# Revit family: Садово-парковая скамейка «Мой Парк NOVA»
name_source: partatom
category: Мебель
revit_build: Autodesk Revit 2017 (Build: 20160225_1515(x64)
units: mm (PartAtom-declared; Revit-internal decimal feet)

## family parameters
Всегда вертикально = Да
Заголовок OmniClass = General Furniture and Specialties
На основе рабочей плоскости = Нет
Номер OmniClass = 23.40.20.00
Общий = Нет
При загрузке вырезать с полостями = Нет
Точка расчета площади = Нет

## types (6) — shared parameters
ADSK_Код изделия = 8464
ADSK_Материал доски = <По категории>
ADSK_Материал опоры = <По категории>
ADSK_Материал фурнитуры = <По категории>
ADSK_Размер_Высота = 750 мм
ADSK_Размер_Высота сидения = 400 мм
ADSK_Размер_Ширина = 650 мм
ADSK_Размер_Ширина сидения = 400 мм
URL = https://hobbyka.ru
Изготовитель = ООО "Хоббика"
Перемычка = Да

## per-type parameters (varying)
| type | ADSK_Размер_Длина | Стоимость | Центральная опора |
| Садово-парковая скамейка «Мой Парк NOVA» 1,2м | 1200 мм | 7877 $ | Нет |
| Садово-парковая скамейка «Мой Парк NOVA» 1,5м | 1500 мм | 8639 $ | Нет |
| Садово-парковая скамейка «Мой Парк NOVA» 1,8м | 1800 мм | 9910 $ | Нет |
| Садово-парковая скамейка «Мой Парк NOVA» 2,0м | 2000 мм | 15627 $ | Да |
| Садово-парковая скамейка «Мой Парк NOVA» 3,0м | 3000 мм | 16627 $ | Да |
| Садово-парковая скамейка «Мой Парк NOVA» Кресло | 600 мм | 6480 $ | Нет |

note: column(s) folded — value = type name in every type: ADSK_Наименование
